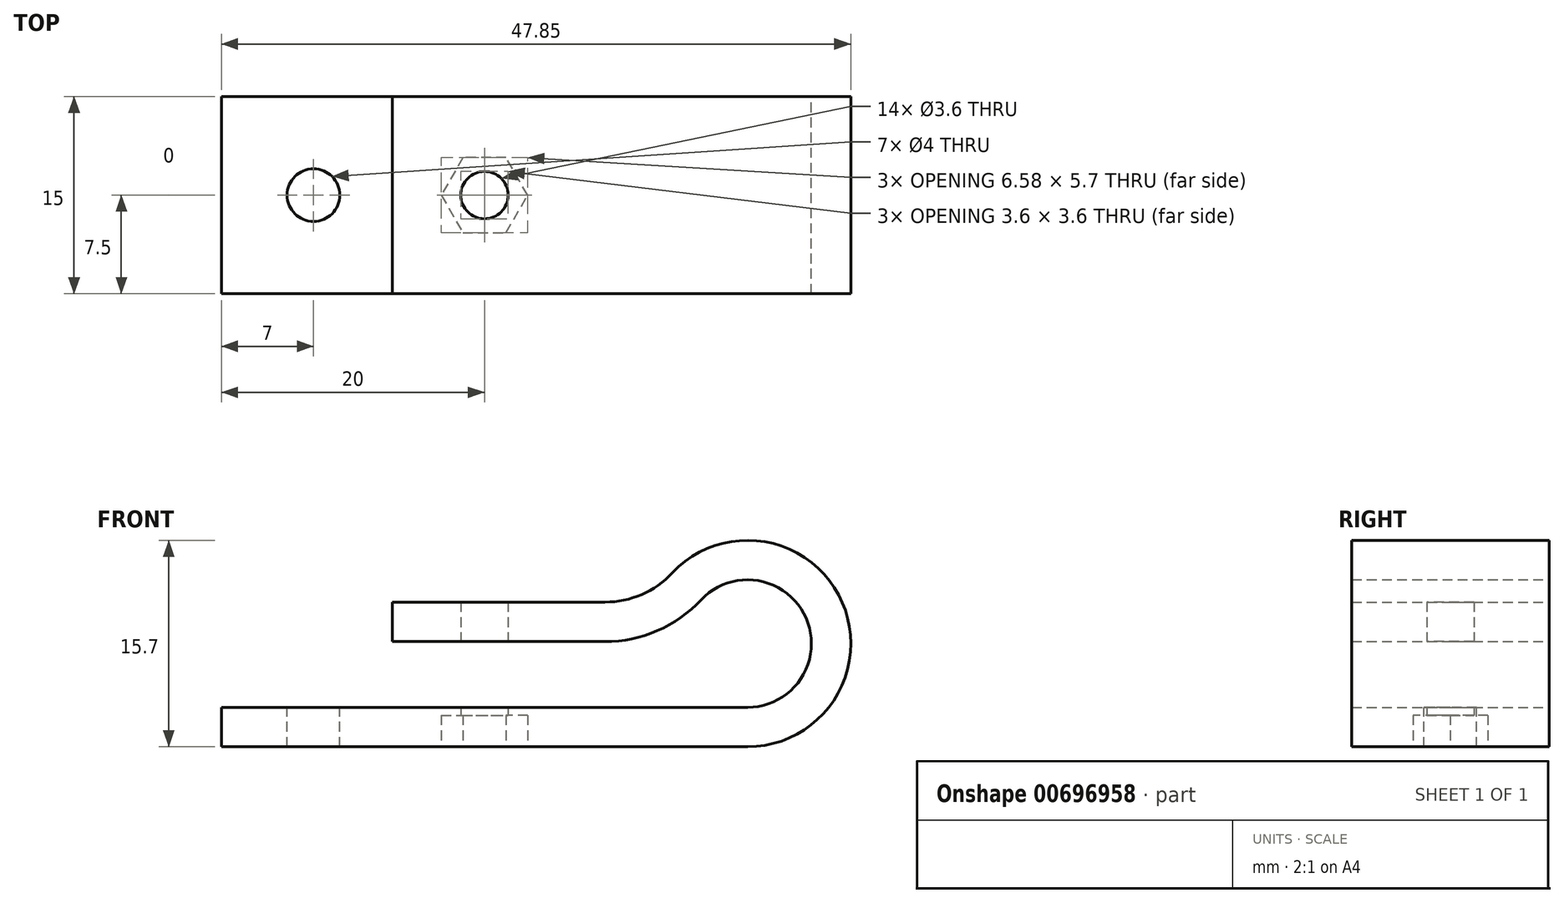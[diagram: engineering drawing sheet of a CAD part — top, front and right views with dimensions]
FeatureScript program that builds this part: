
annotation { "Feature Type Name" : "Feature", "Feature Type Description" : "" }
export const myFeature = defineFeature(function(context is Context, id is Id, definition is map)
    precondition{}
    {
        {
            var Q0;
            Q0=qCreatedBy(makeId("Front.planeOp"),FACE);
            var sketch = newSketch(context, id + "F0", { "sketchPlane" : qUnion([Q0])});
            skLineSegment(sketch, "E0", {"start": v(0, 0) * mm, "end": v(40, 0) * mm});
            skArc(sketch, "E1", {"start": v(40, 0) * mm, "mid": v(44.45, 6.78) * mm, "end": v(36.46, 8.16) * mm});
            skArc(sketch, "E2", {"start": v(29.16, 5) * mm, "mid": v(33.14, 5.83) * mm, "end": v(36.46, 8.16) * mm});
            skLineSegment(sketch, "E3", {"start": v(29.16, 5) * mm, "end": v(13, 5) * mm});
            skLineSegment(sketch, "E4.0", {"start": v(29.16, 8) * mm, "end": v(13, 8) * mm});
            skArc(sketch, "E4.1", {"start": v(29.16, 8) * mm, "mid": v(31.94, 8.58) * mm, "end": v(34.27, 10.22) * mm});
            skArc(sketch, "E4.2", {"start": v(40, -3) * mm, "mid": v(47.2, 7.97) * mm, "end": v(34.27, 10.22) * mm});
            skLineSegment(sketch, "E4.3", {"start": v(0, -3) * mm, "end": v(40, -3) * mm});
            skLineSegment(sketch, "E5", {"start": v(0, 0) * mm, "end": v(0, -3) * mm});
            skLineSegment(sketch, "E6", {"start": v(13, 8) * mm, "end": v(13, 5) * mm});
            skPoint(sketch, "E7.orphan", {"position": v(0, 5) * mm});
            skSolve(sketch);
        }
        {
            var Q0;
            Q0 = qSketchRegion(id + "F0", true);
            extrude(context, id + "F1", {"entities" : qUnion([Q0]), "depth" : 15 * mm, "offsetDistance" : 25 * mm});
        }
        {
            var Q0;
            Q0=makeQuery(id+"F1.opExtrude","SWEPT_FACE",FACE,{"disambiguationData":[OSD([sQuery(id+"F0.wireOp",EDGE,"E4.3")])]});
            var sketch = newSketch(context, id + "F2", { "sketchPlane" : qUnion([Q0])});
            skLineSegment(sketch, "E8", {"start": v(0, 7.5) * mm, "end": v(40, 7.5) * mm, "construction": true});
            skLineSegment(sketch, "E9", {"start": v(20, 15) * mm, "end": v(20, 0) * mm, "construction": true});
            skCircle(sketch, "E10.cCircle", {"center": v(20, 7.5) * mm, "radius": 2.85 * mm, "construction": true});
            skLineSegment(sketch, "E10.0", {"start": v(18.35, 10.35) * mm, "end": v(21.65, 10.35) * mm});
            skLineSegment(sketch, "E10.1", {"start": v(21.65, 10.35) * mm, "end": v(23.3, 7.5) * mm});
            skLineSegment(sketch, "E10.2", {"start": v(23.3, 7.5) * mm, "end": v(21.65, 4.65) * mm});
            skLineSegment(sketch, "E10.3", {"start": v(21.65, 4.65) * mm, "end": v(18.35, 4.65) * mm});
            skLineSegment(sketch, "E10.4", {"start": v(18.35, 4.65) * mm, "end": v(16.7, 7.5) * mm});
            skLineSegment(sketch, "E10.5", {"start": v(16.7, 7.5) * mm, "end": v(18.35, 10.35) * mm});
            skPoint(sketch, "E10.0.midPoint", {"position": v(20, 10.35) * mm});
            skSolve(sketch);
        }
        {
            var Q0;
            Q0=makeQuery(id+"F2.imprint","IMPRINT",FACE,{"disambiguationData":[TD([[makeQuery(id+"F2.imprint","IMPRINT",EDGE,{"derivedFrom":sQuery(id+"F2.wireOp",EDGE,"E10.0")}),-1.0]])]});
            extrude(context, id + "F3", {"entities" : qUnion([Q0]), "operationType" : NewBodyOperationType.REMOVE, "oppositeDirection" : true, "depth" : 2.4 * mm, "offsetDistance" : 25 * mm});
        }
        {
            var Q0;
            Q0=makeQuery(id+"F3.boolean.opBoolean","COPY",FACE,{"derivedFrom":makeQuery(id+"F3.opExtrude","CAP_FACE",FACE,{"disambiguationData":[OSD([sQuery(id+"F2.wireOp",EDGE,"E10.0"),sQuery(id+"F2.wireOp",EDGE,"E10.1"),sQuery(id+"F2.wireOp",EDGE,"E10.2"),sQuery(id+"F2.wireOp",EDGE,"E10.3"),sQuery(id+"F2.wireOp",EDGE,"E10.4"),sQuery(id+"F2.wireOp",EDGE,"E10.5")])],"isStart":false})});
            var sketch = newSketch(context, id + "F4", { "sketchPlane" : qUnion([Q0])});
            skLineSegment(sketch, "E11", {"start": v(20, 10.35) * mm, "end": v(20, 4.65) * mm, "construction": true});
            skLineSegment(sketch, "E12", {"start": v(16.7, 7.5) * mm, "end": v(23.3, 7.5) * mm, "construction": true});
            skCircle(sketch, "E13", {"center": v(20, 7.5) * mm, "radius": 1.8 * mm});
            skSolve(sketch);
        }
        {
            var Q0;
            Q0=makeQuery(id+"F4.imprint","IMPRINT",FACE,{"disambiguationData":[TD([[makeQuery(id+"F4.imprint","IMPRINT",EDGE,{"derivedFrom":sQuery(id+"F4.wireOp",EDGE,"E13")}),1.0]])]});
            extrude(context, id + "F5", {"entities" : qUnion([Q0]), "operationType" : NewBodyOperationType.REMOVE, "endBound" : BoundingType.THROUGH_ALL, "oppositeDirection" : true, "depth" : 25 * mm, "offsetDistance" : 25 * mm});
        }
        {
            var Q0;
            Q0=makeQuery(id+"F1.opExtrude","SWEPT_FACE",FACE,{"disambiguationData":[OSD([sQuery(id+"F0.wireOp",EDGE,"E0")])]});
            var sketch = newSketch(context, id + "F6", { "sketchPlane" : qUnion([Q0])});
            skLineSegment(sketch, "E14", {"start": v(0, -7.5) * mm, "end": v(20, -7.5) * mm, "construction": true});
            skLineSegment(sketch, "E15", {"start": v(7, 0) * mm, "end": v(7, -15) * mm, "construction": true});
            skPoint(sketch, "E16", {"position": v(7, -7.5) * mm});
            skSolve(sketch);
        }
        {
            var Q0;
            Q0=sQuery(id+"F6.wireOp",VERTEX,"E16");
            var Q1;
            Q1=makeQuery(id+"F1.opExtrude","SWEPT_BODY",BODY,{"disambiguationData":[OSD([sQuery(id+"F0.wireOp",EDGE,"E0"),sQuery(id+"F0.wireOp",EDGE,"E1"),sQuery(id+"F0.wireOp",EDGE,"E2"),sQuery(id+"F0.wireOp",EDGE,"E3"),sQuery(id+"F0.wireOp",EDGE,"E4.0"),sQuery(id+"F0.wireOp",EDGE,"E4.1"),sQuery(id+"F0.wireOp",EDGE,"E4.2"),sQuery(id+"F0.wireOp",EDGE,"E4.3"),sQuery(id+"F0.wireOp",EDGE,"E5"),sQuery(id+"F0.wireOp",EDGE,"E6")])]});
            hole(context, id + "F7", {"style" : HoleStyle.SIMPLE, "endStyle" : HoleEndStyle.THROUGH, "holeDiameter" : 4 * mm, "majorDiameter" : 5 * mm, "isTappedThrough" : true, "tappedDepth" : 12 * mm, "tapClearance" : 3, "startFromSketch" : true, "locations" : qUnion([Q0]), "scope" : qUnion([Q1])});
        }
    });
